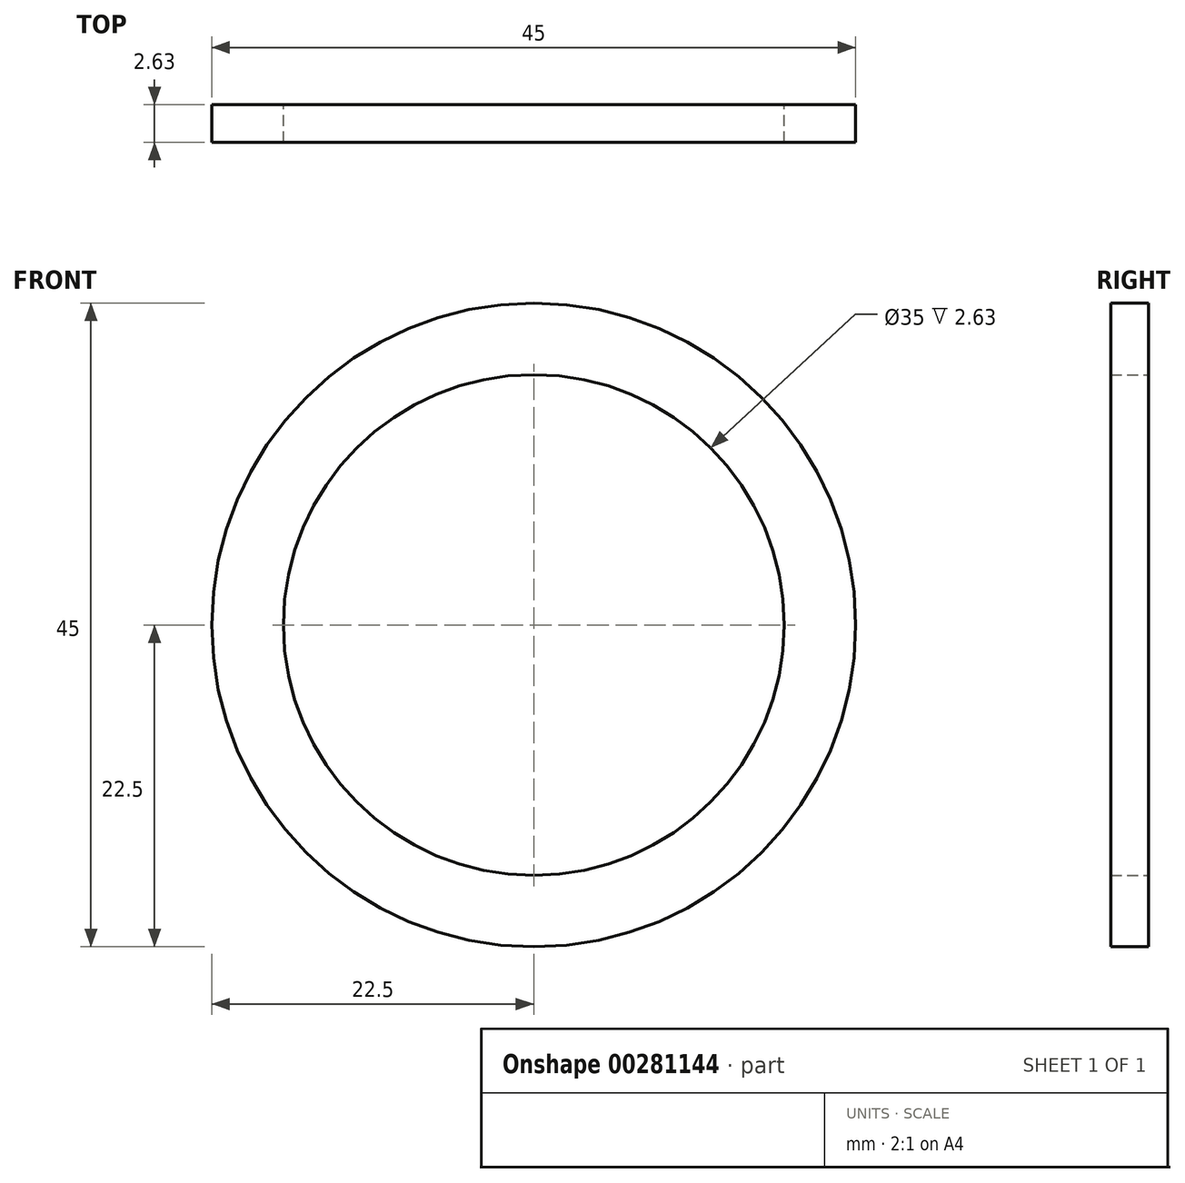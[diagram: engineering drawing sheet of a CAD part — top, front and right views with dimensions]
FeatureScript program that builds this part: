
annotation { "Feature Type Name" : "Feature", "Feature Type Description" : "" }
export const myFeature = defineFeature(function(context is Context, id is Id, definition is map)
    precondition{}
    {
        {
            var Q0;
            Q0=qCreatedBy(makeId("Front.planeOp"),FACE);
            var sketch = newSketch(context, id + "F0", { "sketchPlane" : qUnion([Q0])});
            skCircle(sketch, "E0", {"center": v(0, 0) * mm, "radius": 22.5 * mm});
            skCircle(sketch, "E1", {"center": v(0, 0) * mm, "radius": 17.5 * mm});
            skSolve(sketch);
        }
        {
            var Q0;
            Q0=makeQuery(id+"F0.imprint","IMPRINT",FACE,{"disambiguationData":[TD([[makeQuery(id+"F0.imprint","IMPRINT",EDGE,{"derivedFrom":sQuery(id+"F0.wireOp",EDGE,"E0")}),1.0]])]});
            extrude(context, id + "F1", {"entities" : qUnion([Q0]), "depth" : 2.63 * mm});
        }
    });
